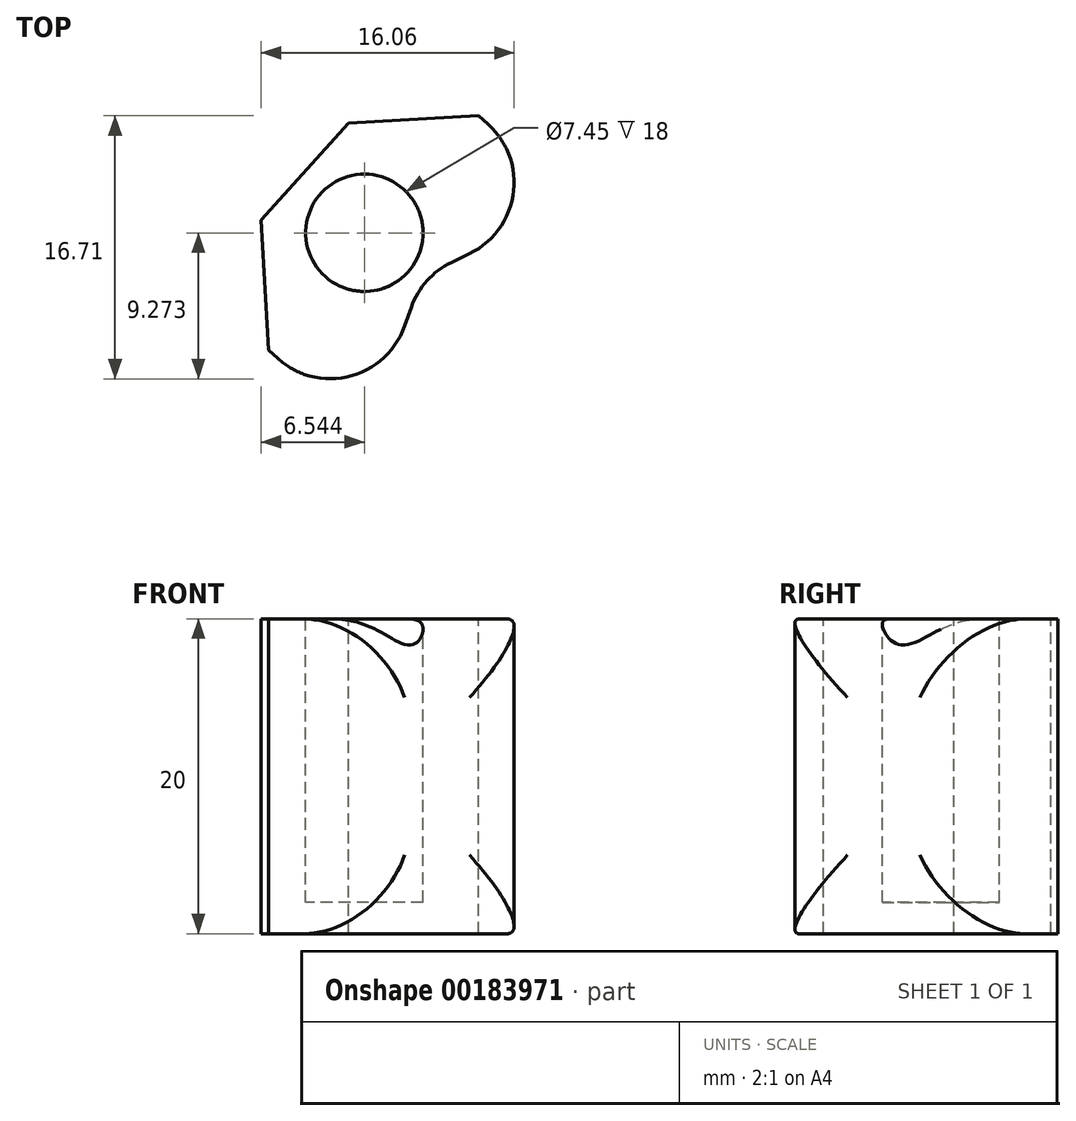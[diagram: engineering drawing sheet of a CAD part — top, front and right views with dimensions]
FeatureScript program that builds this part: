
annotation { "Feature Type Name" : "Feature", "Feature Type Description" : "" }
export const myFeature = defineFeature(function(context is Context, id is Id, definition is map)
    precondition{}
    {
        {
            var Q0;
            Q0=qCreatedBy(makeId("Top.planeOp"),FACE);
            var sketch = newSketch(context, id + "F0", { "sketchPlane" : qUnion([Q0])});
            skLineSegment(sketch, "E0.0", {"start": v(-4.69, 9.76) * mm, "end": v(3.58, 10.21) * mm});
            skLineSegment(sketch, "E0.1", {"start": v(3.58, 10.21) * mm, "end": v(9.76, 4.69) * mm});
            skLineSegment(sketch, "E0.5", {"start": v(-3.58, -10.21) * mm, "end": v(-9.76, -4.69) * mm});
            skLineSegment(sketch, "E0.6", {"start": v(-9.76, -4.69) * mm, "end": v(-10.21, 3.58) * mm});
            skLineSegment(sketch, "E0.7", {"start": v(-10.21, 3.58) * mm, "end": v(-4.69, 9.76) * mm});
            skPoint(sketch, "E0.0.midPoint", {"position": v(-0.55, 9.98) * mm});
            skLineSegment(sketch, "E1", {"start": v(9.76, 4.69) * mm, "end": v(0, 0) * mm});
            skLineSegment(sketch, "E2", {"start": v(0, 0) * mm, "end": v(-3.58, -10.21) * mm});
            skSolve(sketch);
        }
        {
            var Q0;
            Q0=makeQuery(id+"F0.imprint","IMPRINT",FACE,{"disambiguationData":[TD([[makeQuery(id+"F0.imprint","IMPRINT",EDGE,{"derivedFrom":sQuery(id+"F0.wireOp",EDGE,"E0.0")}),-1.0]])]});
            extrude(context, id + "F1", {"entities" : qUnion([Q0]), "oppositeDirection" : true, "depth" : 20 * mm});
        }
        {
            var Q0;
            Q0=makeQuery(id+"F1.opExtrude","SWEPT_FACE",FACE,{"disambiguationData":[OSD([sQuery(id+"F0.wireOp",EDGE,"E2")])]});
            var Q1;
            Q1=makeQuery(id+"F1.opExtrude","SWEPT_FACE",FACE,{"disambiguationData":[OSD([sQuery(id+"F0.wireOp",EDGE,"E1")])]});
            fillet(context, id + "F2", {"entities" : qUnion([Q0, Q1]), "radius" : 5 * mm, "tangentPropagation" : true, "allowEdgeOverflow" : false});
        }
        {
            var Q0;
            Q0=makeQuery(id+"F1.opExtrude","CAP_FACE",FACE,{"disambiguationData":[OSD([sQuery(id+"F0.wireOp",EDGE,"E0.0"),sQuery(id+"F0.wireOp",EDGE,"E0.1"),sQuery(id+"F0.wireOp",EDGE,"E0.5"),sQuery(id+"F0.wireOp",EDGE,"E0.6"),sQuery(id+"F0.wireOp",EDGE,"E0.7"),sQuery(id+"F0.wireOp",EDGE,"E1"),sQuery(id+"F0.wireOp",EDGE,"E2")])],"isStart":true});
            var sketch = newSketch(context, id + "F3", { "sketchPlane" : qUnion([Q0])});
            skCircle(sketch, "E3", {"center": v(-3.67, 2.77) * mm, "radius": 3.73 * mm});
            skSolve(sketch);
        }
        {
            var Q0;
            {var subQ0=sQuery(id+"F3.wireOp",EDGE,"E3");var subQ1=sQuery(id+"F0.wireOp",EDGE,"E2");var subQ2=sQuery(id+"F0.wireOp",EDGE,"E1");var subQ3=makeQuery(id+"F1.opExtrude","CAP_FACE",FACE,{"disambiguationData":[OSD([sQuery(id+"F0.wireOp",EDGE,"E0.0"),sQuery(id+"F0.wireOp",EDGE,"E0.1"),sQuery(id+"F0.wireOp",EDGE,"E0.5"),sQuery(id+"F0.wireOp",EDGE,"E0.6"),sQuery(id+"F0.wireOp",EDGE,"E0.7"),subQ2,subQ1])],"isStart":true});var subQ6=makeQuery(id+"F2.opFillet","BLEND_EDGE",EDGE,{"blendedFrom":[makeQuery(id+"F1.opExtrude","CAP_EDGE",EDGE,{"disambiguationData":[OSD([subQ1])],"isStart":true}),subQ3],"blendedInto":[subQ3]});var subQ7=makeQuery(id+"F3.imprint","INTERSECT",VERTEX,{"derivedFrom":[subQ6,subQ0]});Q0=makeQuery(id+"F3.imprint","IMPRINT",FACE,{"disambiguationData":[TD([[makeQuery(id+"F3.imprint","IMPRINT",EDGE,{"disambiguationData":[TD([[subQ7,-1.0]])],"derivedFrom":subQ0}),1.0]])]});}
            var Q1;
            {var subQ0=sQuery(id+"F3.wireOp",EDGE,"E3");var subQ1=sQuery(id+"F0.wireOp",EDGE,"E2");var subQ2=sQuery(id+"F0.wireOp",EDGE,"E1");var subQ3=makeQuery(id+"F1.opExtrude","CAP_FACE",FACE,{"disambiguationData":[OSD([sQuery(id+"F0.wireOp",EDGE,"E0.0"),sQuery(id+"F0.wireOp",EDGE,"E0.1"),sQuery(id+"F0.wireOp",EDGE,"E0.5"),sQuery(id+"F0.wireOp",EDGE,"E0.6"),sQuery(id+"F0.wireOp",EDGE,"E0.7"),subQ2,subQ1])],"isStart":true});var subQ6=makeQuery(id+"F2.opFillet","BLEND_EDGE",EDGE,{"blendedFrom":[makeQuery(id+"F1.opExtrude","CAP_EDGE",EDGE,{"disambiguationData":[OSD([subQ1])],"isStart":true}),subQ3],"blendedInto":[subQ3]});var subQ7=makeQuery(id+"F3.imprint","INTERSECT",VERTEX,{"derivedFrom":[subQ6,subQ0]});Q1=makeQuery(id+"F3.imprint","IMPRINT",FACE,{"disambiguationData":[TD([[makeQuery(id+"F3.imprint","IMPRINT",EDGE,{"disambiguationData":[TD([[subQ7,1.0]])],"derivedFrom":subQ0}),1.0]])]});}
            extrude(context, id + "F4", {"entities" : qUnion([Q0, Q1]), "operationType" : NewBodyOperationType.REMOVE, "oppositeDirection" : true, "depth" : 18 * mm});
        }
    });
